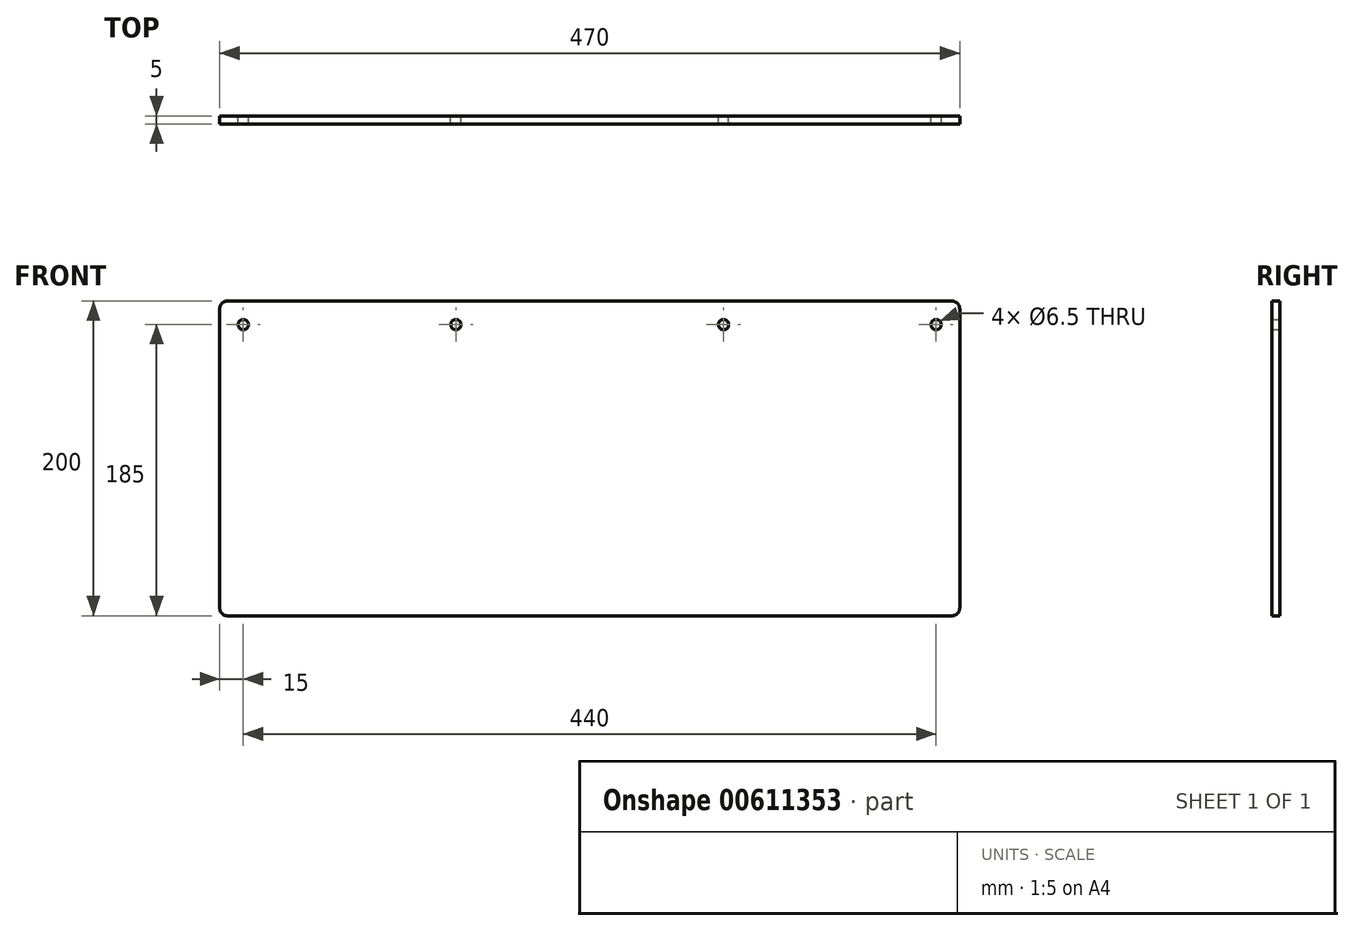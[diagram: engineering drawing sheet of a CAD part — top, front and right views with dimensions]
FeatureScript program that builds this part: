
annotation { "Feature Type Name" : "Feature", "Feature Type Description" : "" }
export const myFeature = defineFeature(function(context is Context, id is Id, definition is map)
    precondition{}
    {
        {
            var Q0;
            Q0=qCreatedBy(makeId("Front.planeOp"),FACE);
            var sketch = newSketch(context, id + "F0", { "sketchPlane" : qUnion([Q0])});
            skLineSegment(sketch, "E0.bottom", {"start": v(0, 0) * mm, "end": v(470, 0) * mm});
            skLineSegment(sketch, "E0.top", {"start": v(0, 200) * mm, "end": v(470, 200) * mm});
            skLineSegment(sketch, "E0.left", {"start": v(0, 0) * mm, "end": v(0, 200) * mm});
            skLineSegment(sketch, "E0.right", {"start": v(470, 0) * mm, "end": v(470, 200) * mm});
            skCircle(sketch, "E1", {"center": v(15, 185) * mm, "radius": 3.25 * mm});
            skCircle(sketch, "E2", {"center": v(150, 185) * mm, "radius": 3.25 * mm});
            skCircle(sketch, "E3", {"center": v(320, 185) * mm, "radius": 3.25 * mm});
            skCircle(sketch, "E4", {"center": v(455, 185) * mm, "radius": 3.25 * mm});
            skSolve(sketch);
        }
        {
            var Q0;
            Q0=makeQuery(id+"F0.imprint","IMPRINT",FACE,{"disambiguationData":[TD([[makeQuery(id+"F0.imprint","IMPRINT",EDGE,{"derivedFrom":sQuery(id+"F0.wireOp",EDGE,"E0.bottom")}),1.0]])]});
            extrude(context, id + "F1", {"entities" : qUnion([Q0]), "depth" : 5 * mm, "offsetDistance" : 25 * mm});
        }
        {
            var Q0;
            Q0=makeQuery(id+"F1.opExtrude","SWEPT_EDGE",EDGE,{"disambiguationData":[OSD([sQuery(id+"F0.wireOp",EDGE,"E0.top"),sQuery(id+"F0.wireOp",EDGE,"E0.left")])]});
            var Q1;
            Q1=makeQuery(id+"F1.opExtrude","SWEPT_EDGE",EDGE,{"disambiguationData":[OSD([sQuery(id+"F0.wireOp",EDGE,"E0.bottom"),sQuery(id+"F0.wireOp",EDGE,"E0.right")])]});
            var Q2;
            Q2=makeQuery(id+"F1.opExtrude","SWEPT_EDGE",EDGE,{"disambiguationData":[OSD([sQuery(id+"F0.wireOp",EDGE,"E0.bottom"),sQuery(id+"F0.wireOp",EDGE,"E0.left")])]});
            var Q3;
            Q3=makeQuery(id+"F1.opExtrude","SWEPT_EDGE",EDGE,{"disambiguationData":[OSD([sQuery(id+"F0.wireOp",EDGE,"E0.top"),sQuery(id+"F0.wireOp",EDGE,"E0.right")])]});
            fillet(context, id + "F2", {"entities" : qUnion([Q0, Q1, Q2, Q3]), "radius" : 5 * mm, "tangentPropagation" : true, "allowEdgeOverflow" : false});
        }
    });
